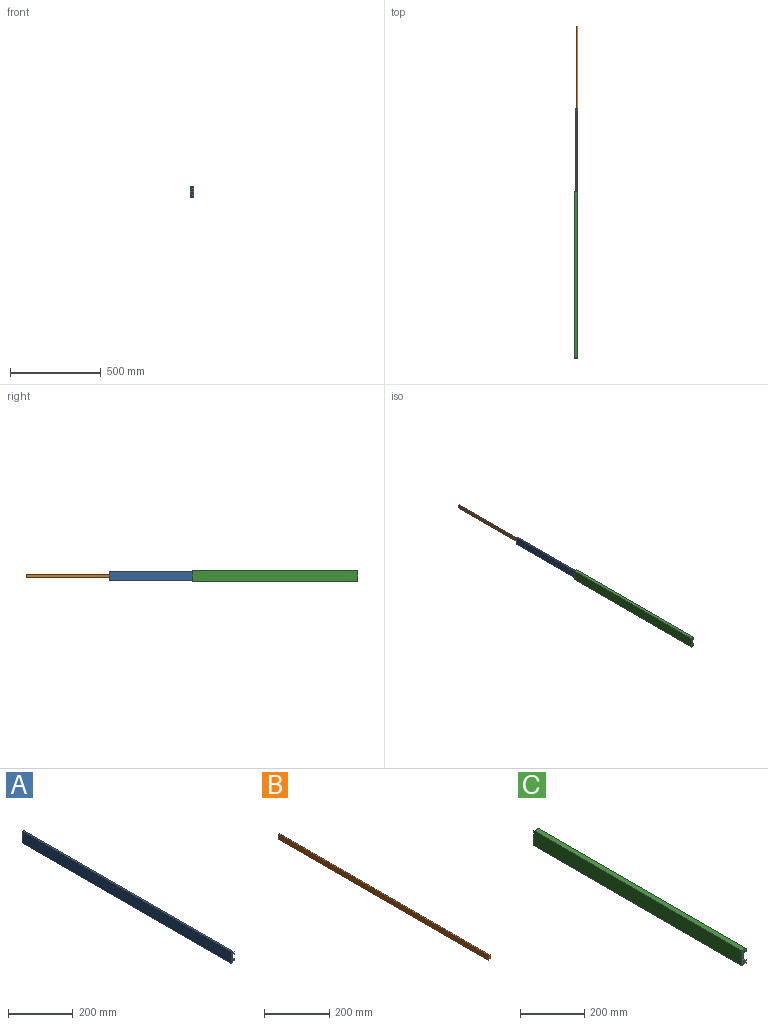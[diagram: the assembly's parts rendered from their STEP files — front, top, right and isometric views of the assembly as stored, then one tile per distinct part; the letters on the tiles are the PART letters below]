
ASSEMBLY  parts=3 mates=2
PART A: 14 faces, bbox 12.7x914.4x44.5 mm
  f0: plane 914.4x6.35mm, normal (0,0,1), area 5806.4mm2, adj f1,f11,f12,f13
  f1: plane 914.4x6.35mm, normal (1,0,0), area 5806.4mm2, adj f0,f2,f12,f13
  f2: plane 914.4x6.35mm, normal (0,0,1), area 5806.4mm2, adj f1,f3,f12,f13
  f3: plane 914.4x44.45mm, normal (-1,0,0), area 40645.1mm2, adj f2,f4,f12,f13
  f4: plane 914.4x6.35mm, normal (0,0,-1), area 5806.4mm2, adj f3,f5,f12,f13
  f5: plane 914.4x6.35mm, normal (1,0,0), area 5806.4mm2, adj f4,f6,f12,f13
  f6: plane 914.4x6.35mm, normal (0,0,-1), area 5806.4mm2, adj f5,f7,f12,f13
  f7: plane 914.4x8.33mm, normal (1,0,0), area 7616.1mm2, adj f6,f8,f12,f13
  f8: plane 914.4x7.94mm, normal (-0.24,0,0.97), area 7480.2mm2, adj f7,f9,f12,f13
  f9: plane 914.4x19.05mm, normal (1,0,0), area 17419.3mm2, adj f8,f10,f12,f13
  f10: plane 914.4x7.94mm, normal (-0.24,0,-0.97), area 7480.2mm2, adj f9,f11,f12,f13
  f11: plane 914.4x8.33mm, normal (1,0,0), area 7616.1mm2, adj f0,f10,f12,f13
  f12: plane 44.45x12.7mm, normal (0,-1,0), area 348.4mm2, adj f0,f1,f2,f3,f4,f5,f6,f7
  f13: plane 44.45x12.7mm, normal (0,1,0), area 348.4mm2, adj f0,f1,f2,f3,f4,f5,f6,f7
PART B: 6 faces, bbox 7.9x914.4x19.1 mm
  f0: plane 914.4x19.05mm, normal (-1,0,0), area 17419.3mm2, adj f1,f3,f4,f5
  f1: plane 914.4x7.94mm, normal (0.24,0,-0.97), area 7480.2mm2, adj f0,f2,f4,f5
  f2: plane 914.4x15.09mm, normal (1,0,0), area 13800mm2, adj f1,f3,f4,f5
  f3: plane 914.4x7.94mm, normal (0.24,0,0.97), area 7480.2mm2, adj f0,f2,f4,f5
  f4: plane 19.05x7.94mm, normal (0,-1,0), area 135.5mm2, adj f0,f1,f2,f3
  f5: plane 19.05x7.94mm, normal (0,1,0), area 135.5mm2, adj f0,f1,f2,f3
PART C: 14 faces, bbox 19.1x914.4x57.2 mm
  f0: plane 914.4x6.35mm, normal (-1,0,0), area 5806.4mm2, adj f1,f11,f12,f13
  f1: plane 914.4x6.35mm, normal (0,0,-1), area 5806.4mm2, adj f0,f2,f12,f13
  f2: plane 914.4x12.7mm, normal (1,0,0), area 11612.9mm2, adj f1,f3,f12,f13
  f3: plane 914.4x19.05mm, normal (0,0,1), area 17419.3mm2, adj f2,f4,f12,f13
  f4: plane 914.4x57.15mm, normal (-1,0,0), area 52258mm2, adj f3,f5,f12,f13
  f5: plane 914.4x19.05mm, normal (0,0,-1), area 17419.3mm2, adj f4,f6,f12,f13
  f6: plane 914.4x12.7mm, normal (1,0,0), area 11612.9mm2, adj f5,f7,f12,f13
  f7: plane 914.4x6.35mm, normal (0,0,1), area 5806.4mm2, adj f6,f8,f12,f13
  f8: plane 914.4x6.35mm, normal (-1,0,0), area 5806.4mm2, adj f7,f9,f12,f13
  f9: plane 914.4x6.35mm, normal (0,0,1), area 5806.4mm2, adj f8,f10,f12,f13
  f10: plane 914.4x44.45mm, normal (1,0,0), area 40645.1mm2, adj f9,f11,f12,f13
  f11: plane 914.4x6.35mm, normal (0,0,-1), area 5806.4mm2, adj f0,f10,f12,f13
  f12: plane 57.15x19.05mm, normal (0,-1,0), area 604.8mm2, adj f0,f1,f2,f3,f4,f5,f6,f7
  f13: plane 57.15x19.05mm, normal (0,1,0), area 604.8mm2, adj f0,f1,f2,f3,f4,f5,f6,f7
PLACE A t=(0,457.2,0)mm
PLACE B t=(0,914.4,0)mm
PLACE C at identity fixed
MATE slider A.f12 <-> B.f4  axis (0,-1,0) through (-7.94,-457.2,9.52)mm
MATE slider C.f12 <-> A.f12  axis (0,-1,0) through (-12.7,-914.4,22.22)mm
